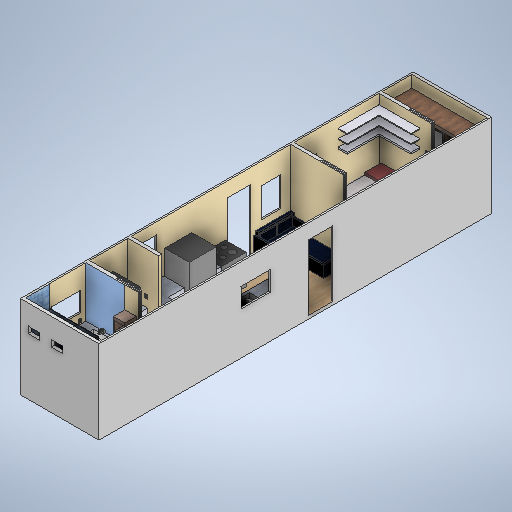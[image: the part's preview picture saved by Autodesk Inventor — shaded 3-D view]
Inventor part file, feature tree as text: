
AUTODESK INVENTOR PART (.ipt)
format: ipt  version: 2025 (Build 290162000, 162)  size: 1,956,352 bytes
history: native  units: in
note: dims shown in document units (in); Inventor stores cm internally (conversion verified against a paired STEP export)
features: extrude x58, sketch x40, chamfer x8, other x6, fillet x5
ambient origin geometry x8: Origin, YZ Plane, XZ Plane, XY Plane, X Axis, Y Axis, Z Axis, Center Point
bodies: Solid1 (feature_tree)
feature tree (117):
  extrude  "House shell -outer"  Depth=480.0in
  extrude  "House shell -inner"  Depth=2.0in
  other  "Layout"
  extrude  "Height -all counters"  Depth=2.0in
  extrude  "Kitchen sink depth"  Depth=98.0in TaperAngle=0.0deg
  extrude  "Bathroom sink depth"  Depth=30.0in
  extrude  "Height -Kitchen pantry, w/d, bathroom linen, shower stall"  Depth=19.0in
  extrude  "Interior walls"  Depth=47.25in
  extrude  "Fridge"  Depth=21.0in
  extrude  "Couch -back"  Depth=4.0in
  extrude  "Couch -arms"  Depth=4.0in
  extrude  "Chouch -cushions, coffee table"  Depth=4.0in
  fillet  "Couch -cusions round"  Radius=4.0in
  extrude  "Couch -back cushions"  Depth=4.0in
  fillet  "Couch -back cushions round"  [1 undecoded]
  extrude  "Back of house -back door, bedroom window, living room window, kitchen window, bathroom window"  Depth=36.0in
  extrude  "Bathroom shower windows -exterior"  Depth=25.0in
  extrude  "Front of house -front door, kitchen sink window"  TaperAngle=0.0deg  [1 undecoded]
  extrude  "Coffee table -legs1"  Depth=20.0in
  extrude  "Coffee table -legs2"  TaperAngle=0.0deg  [1 undecoded]
  extrude  "Shower wall -without windows"  TaperAngle=0.0deg  [1 undecoded]
  extrude  "Shower wall -with windows"  Depth=30.0in
  extrude  "Bathroom shower windows -interior"  Depth=1.0in
  extrude  "Stove top -surface"  Depth=36.0in
  extrude  "Stove front"  Depth=40.0in
  extrude  "Stove-top -burners"  Depth=2.0in
  extrude  "Kitchen pantry - shelves"  Depth=18.0in
  extrude  "Kitchen counter -hang over"  Depth=30.0in
  extrude  "Toilet -block"  Depth=28.0in
  fillet  "Toilet -round"  Radius=3.0in
  extrude  "Toilet -shaape"  Depth=14.0in
  extrude  "Bathroom mirror"  Depth=24.0in
  extrude  "Bathroom linen - shelving"  Depth=3.0in
  extrude  "Bathroom light switch"  Depth=24.0in
  chamfer  "Bathroom light switch -outside"  Distance=4.0in
  chamfer  "Bethroom light switch -sockets"  [1 undecoded]
  extrude  "Front door light switch"  Depth=36.0in
  chamfer  "Front door light switch -outside"  [1 undecoded]
  chamfer  "Front door light switch -sockets"  Distance=60.0in
  extrude  "Dishwasher -front"  Depth=36.0in
  extrude  "Dishwasher -side"  Depth=36.0in
  other  "Kitchen sink faucet"
  extrude  "Kitchen sink faucet -block"  Depth=36.0in
  extrude  "Kitchen sink faucet -depth"  Depth=36.0in
  other  "Kitchen sink faucet -bottom round"
  other  "Kitchen sink faucet -top round"
  extrude  "Kitchen sink knobs -block"  Depth=1.0in
  extrude  "Kitchen sink knobs -shape"  Depth=1.0in
  extrude  "Kitchen sink knobs -depth"  Depth=1.0in
  fillet  "Kitchen sink knobs -round"  Radius=1.0in
  extrude  "Closet organizer -depth"  Depth=13.5in
  other  "Closet organizer"
  extrude  "Closet organizer -shelves"  Depth=0.5in
  sketch  "Sketch59"  dims[d140=28.0in d141=4.0in d143=0.0in d144=30.2112in d148=0.0in d149=60.0in d154=0.06in d155=0.06in d156=0.06in d157=0.06in d158=1.0in d159=1.0in d160=1.0in d161=1.0in d162=13.5in d163=0.5in d164=0.5in d165=0.0in d166=0.0in d167=36.0in d168=0.0in d169=26.0in d170=0.0in d171=30.0in d172=0.0in d173=72.0in d174=0.0in d175=98.0in d176=0.0in d177=16.0in d180=30.0in d181=0.0in d184=65.0in d185=0.0in d186=3.0in d189=2.0in d190=2.0in d192=24.5in d194=8.0in d199=22.0in d202=19.0in d204=28.0in d205=0.0in d206=24.0in d207=0.0in d208=15.0in d209=0.0in d210=25.0in d211=0.0in d212=3.0in d238=24.0in d239=36.0in d240=48.0in d241=36.0in d242=24.0in d243=48.0in d244=2.0in d245=0.0in d246=14.0in d247=8.0in d248=8.0in d249=14.0in d250=1.0in d251=0.0in d252=9.5in d257=36.0in d258=24.0in d259=48.0in d260=2.0in d261=0.0in d267=30.0in d268=80.0in d269=0.0in d271=0.5in d272=0.0in d273=0.5in d274=0.0in d277=14.0in d278=14.0in d279=30.0in d280=0.5in d281=0.0in d282=0.5in d283=0.0in d288=20.0in d289=20.0in d290=26.0in d291=26.0in d292=3.0in d293=0.0in d294=30.0in d295=0.5in d296=0.0in d297=8.0in d298=0.0in d299=1.0in d300=0.0in d301=0.25in d302=0.0in d303=13.0in d304=13.0in d305=13.0in d306=13.0in d307=5.0in d308=2.0in d309=2.0in d310=2.0in d311=2.0in d312=2.0in d313=2.0in d314=12.0in d315=0.0in d316=1.0in d317=1.0in d318=1.0in d320=1.0in d321=1.0in d322=1.0in d323=1.0in d325=4.0in d326=11.0in d327=11.0in d328=11.0in d329=11.0in d330=11.0in d331=12.0in d332=0.0in d333=1.5in d334=1.5in d335=1.0in d336=106.0in d337=108.37in d338=0.0in d339=0.0in d340=4.5in d341=4.5in d342=1.0in d343=1.0in d344=1.156in d345=1.156in d346=1.156in d347=1.156in d349=0.0in d350=0.0in d351=0.5in d352=0.0in d353=0.125in d354=0.125in d355=45.0deg d356=0.075in d357=0.125in d358=45.0deg d359=0.5in d360=0.5in d361=0.5in d362=0.5in d363=2.0in d364=0.65in d365=0.4in d366=0.4in d367=0.4in d368=0.4in d370=48.0in d371=5.0in d455=0.5in d456=0.0in d457=0.075in d458=0.125in d459=45.0deg d460=0.125in d461=0.125in d462=45.0deg d463=0.4in d464=0.4in d465=0.4in d466=0.4in d467=2.0in d468=1.0in d469=0.65in d470=0.65in d471=0.6in d472=4.5in d473=4.5in d474=24.0in d475=35.0in d476=0.5in d477=0.0in d478=24.0in d479=35.0in d480=0.05in d481=0.0in d482=9.0in d483=0.0in d484=1.0in d485=2.0in d486=2.0in d487=2.0in d488=4.0in d489=1.0in d490=1.0in d491=1.0in d492=0.0in d493=0.0in d494=2.0in d495=16.5in d497=0.0in d498=2.0in d499=2.5in d500=2.0in d501=2.0in d502=2.0in d503=2.5in d504=0.0in d505=3.0in d506=0.0in d507=1.0in d508=0.5in d509=0.5in d510=3.0in d511=0.0in d512=2.5in d513=0.0in d516=0.35in d517=1.0in d518=20.0in d519=20.0in d520=2.0in d521=2.0in d522=12.0in d523=0.0in d524=0.5in d525=0.7in d530=84.0in d531=0.0in d539=2.0in d540=2.0in d542=14.0in d543=14.0in d544=14.0in d546=4.0in d548=2.0in d550=2.0in d551=10.0in d553=1.0in d554=1.0in d556=2.0in d557=12.0in d558=22.0in d559=0.0in d560=0.05in d561=0.0in d567=1.0in d568=50.0in d569=11.0in d570=2.0in d571=1.0in d572=10.0in d573=8.0in d574=12.0in d575=50.0in d576=50.0in d577=50.0in d578=0.0in d579=11.0in d580=0.0in d582=2.0in d583=6.0in d584=8.0in d585=0.0in d586=10.25in d587=1.0in d589=2.0in d590=1.5in d591=0.0in d592=0.125in d593=1.0in d594=0.75in d595=2.0in d596=0.0in d597=2.0in d598=2.0in d599=4.0in d600=2.0in d601=0.0in d602=1.0in d603=1.0in d604=4.0in d605=1.0in d606=0.0in d607=0.0in d608=0.65in d609=0.65in d610=0.4in d611=0.4in d612=0.6in d613=0.4in d614=0.4in d615=1.0in d616=2.0in d617=4.5in d618=4.5in d620=0.0in d621=0.5in d622=48.0in d623=0.65in d624=0.6in d625=1.0in d626=1.0in d627=1.0in d628=1.0in d629=1.0in d630=1.0in d631=1.0in d632=10.0in d633=0.075in d634=0.125in d635=45.0deg d636=0.125in d637=0.125in d638=45.0deg d639=0.65in d642=1.0in d643=0.65in d647=0.4in d648=1.0in d652=0.4in d653=1.0in d655=1.0in d656=2.0in d662=0.0in d663=0.5in d666=0.125in d667=0.125in d668=45.0deg d669=0.075in d670=0.125in d671=45.0deg d672=1.0in d674=0.6in d675=0.6in d676=4.5in d677=48.0in d679=18.0in d680=3.0in d686=3.0in d687=8.0in d688=15.0in d692=0.0in d693=0.5in d694=0.0in d695=4.5in d696=3.0in d697=1.5in d698=1.5in d699=1.5in d703=0.0in d704=1.25in d705=1.25in d706=0.5in d707=0.0in d708=0.75in d709=0.75in d710=0.75in d711=0.75in d712=1.0in d713=1.0in d714=2.0in d715=6.0in d716=0.75in d717=0.75in d718=0.75in d719=0.75in d720=1.0in d721=1.0in d722=1.25in d723=1.25in d724=0.0in d725=1.5in d726=2.1268in d727=35.5432in d728=4.5in d729=3.0in d731=0.0in d732=0.5in d733=9.5647in d734=1.0in d735=1.0in d736=1.0in d737=1.0in d740=0.75in d741=0.75in d742=0.75in d743=0.75in d744=1.0in d745=1.0in d746=1.0in d747=1.0in d750=0.0in d751=1.5in d753=4.5in d754=3.0in d756=0.0in d757=0.5in d758=1.25in d759=1.25in d760=3.0in d761=3.0in d764=0.75in d765=0.75in d766=0.75in d767=0.75in d768=1.0in d769=1.0in d770=1.0in d771=1.0in d772=1.25in d773=1.25in d774=0.0in d775=1.5in d777=4.5in d778=3.0in d780=0.0in d781=0.5in d782=3.0in d783=10.0in d786=0.75in d787=0.75in d788=0.75in d789=0.75in d790=1.0in d791=1.0in d792=1.0in d793=1.0in d794=1.25in d795=1.25in d796=0.0in d797=1.5in d799=4.5in d800=3.0in d802=0.0in d803=0.5in d806=0.75in d807=0.75in d808=0.75in d809=0.75in d810=1.0in d811=1.0in d812=1.0in d813=1.0in d814=1.25in d815=1.25in d816=0.0in d817=1.5in d819=4.5in d820=3.0in d822=0.0in d823=0.5in d824=6.0in d825=20.0in d826=6.0in d827=6.0in d830=0.75in d831=0.75in d832=0.75in d833=0.75in d834=1.0in d835=1.0in d836=1.0in d837=1.0in d838=1.25in d839=1.25in d840=0.0in d841=1.5in d843=4.5in d844=3.0in d846=0.0in d847=0.5in d848=6.0in d849=15.0in d852=0.75in d853=0.75in d854=0.75in d855=0.75in d856=1.0in d857=1.0in d858=1.0in d859=1.0in d860=1.25in d861=1.25in d862=0.0in d863=1.5in d865=4.5in d866=3.0in d868=0.0in d869=0.5in d870=4.0in d872=0.0in d874=24.0in d875=36.0in d876=36.0in d877=36.0in d882=28.0in d883=80.0in d885=24.0in d887=13.0in d888=3.0in d891=1.5in d895=106.0in d896=4.5in d897=40.0in d898=34.0in d899=7.0in d900=4.0in d901=16.0in d902=2.7558in d903=30.0in d904=0.0in d906=24.0in d907=0.5in d908=59.5in d909=0.5in d910=0.5in d911=92.0in d913=0.0in d915=2.25in d916=0.0in d917=2.0in d918=0.0in d919=0.0in d920=0.0in d921=25.25in d922=25.25in d923=25.25in d924=23.25in d925=23.25in d926=23.25in d928=12.0in d929=12.0in d930=12.0in d932=3.0in d933=3.0in d934=0.0in d935=0.0in d937=0.0in d939=1.0in d940=4.0in d943=2.2419in d944=2.2472in d945=0.0in d946=59.5in d947=2.0in d948=11.0in d949=12.0in d950=22.0in d951=0.0in d952=120.0in d953=68.5in d954=36.0in d955=87.0in d956=69.5in d957=69.5in d526=0.0in d527=0.0in]
  extrude  "Closet organizer -drawers"  Depth=0.5in
  extrude  "Closet organizer -rod"  TaperAngle=0.0deg  [1 undecoded]
  extrude  "Bed -block"  TaperAngle=0.0deg  [1 undecoded]
  fillet  "Bed - round"  Radius=36.0in
  extrude  "Pillows"  Depth=26.0in TaperAngle=0.0deg
  other  "Bedroom shelves"
  extrude  "Bedroom shelves -with window"  Depth=30.0in TaperAngle=0.0deg
  extrude  "Bedroom shelves -without window"  Depth=72.0in TaperAngle=0.0deg
  extrude  "Bathroom sink faucet -block"  Depth=98.0in TaperAngle=0.0deg
  extrude  "Bathroom sink faucet -shape"  Depth=16.0in
  chamfer  "Bedroom light switch -outside"  Distance=30.0in
  chamfer  "Bedroom light switch -sockets"  Distance=65.0in
  chamfer  "Closet light switch -outside"  Distance=3.0in
  chamfer  "Closet light switch -sockets"  Distance=2.0in
  extrude  "Bathroom outlet"  Depth=2.0in
  sketch  "Sketch1"  dims[d0=96.0in d1=480.0in]
  sketch  "Sketch2"  dims[d2=102.0in d3=0.0in d4=2.0in]
  sketch  "Sketch7"  dims[d5=2.0in d6=3.5in]
  sketch  "Sketch8"  dims[d7=3.5in d8=98.0in d9=0.0in]
  sketch  "Sketch9"  dims[d12=60.0in d13=30.0in]
  sketch  "Sketch11"  dims[d14=29.0in d15=19.0in]
  sketch  "Sketch12"  dims[d17=0.0in d18=47.25in]
  sketch  "Sketch13"  dims[d19=21.0in d20=13.375in]
  sketch  "Sketch14"  dims[d21=20.5in d22=4.0in]
  sketch  "Sketch15"  dims[d23=24.0in d24=4.0in]
  sketch  "Sketch16"  dims[d25=29.0in d26=33.0in d34=4.0in]
  sketch  "Sketch17"  dims[d35=4.0in d37=80.0in d38=0.0in]
  sketch  "Sketch18"  dims[d39=24.0in d40=36.0in]
  sketch  "Sketch19"  dims[d50=25.0in d51=25.0in]
  sketch  "Sketch20"  dims[d52=20.0in d53=0.0in]
  sketch  "Sketch21"  dims[d60=14.0in d61=20.0in]
  sketch  "Sketch22"  dims[d66=30.0in d68=0.0in]
  sketch  "Sketch26"  dims[d79=33.0in d80=30.0in]
  sketch  "Sketch28"  dims[d82=1.0in d83=1.0in]
  sketch  "Sketch30"  dims[d85=0.0in d87=36.0in]
  sketch  "Sketch31"  dims[d89=4.5in d94=40.0in]
  sketch  "Sketch32"  dims[d99=25.0in d101=2.0in]
  sketch  "Sketch33"  dims[d102=18.0in d103=33.0in]
  sketch  "Sketch41"  dims[d104=4.0in d106=30.0in]
  sketch  "Sketch42"  dims[d107=25.0in d109=28.0in d111=8.0in d114=3.0in]
  sketch  "Sketch43"  dims[d115=14.0in d116=33.0in]
  sketch  "Sketch45"  dims[d117=24.0in d118=24.0in]
  sketch  "Sketch49"  dims[d128=1.5in]
  sketch  "Sketch50"  dims[d129=1.25in]
  extrude  "Closet light switch"  Depth=24.5in
  sketch  "Sketch25"  dims[d75=0.0in d76=0.0in]
  sketch  "Sketch47"  dims[d119=3.0in d120=3.0in]
  sketch  "Sketch48"  dims[d126=24.0in d127=28.5in]
  sketch  "Sketch51"  dims[d132=1.5in]
  sketch  "Sketch52"  dims[d133=28.5in]
  sketch  "Sketch53"  dims[d134=1.5in]
  sketch  "Sketch54"  dims[d135=28.5in]
  sketch  "Sketch55"  dims[d137=1.25in]
  sketch  "Sketch56"  dims[d138=0.0in]
  sketch  "Sketch57"  dims[d139=1.25in]
  extrude  "Bedroom light switch"  Depth=8.0in
  extrude  "Laundry room outlet"  Depth=22.0in
  extrude  "Kitchen outlet1"  Depth=19.0in
  extrude  "Kitchtn outlet2"  Depth=28.0in TaperAngle=0.0deg
  extrude  "Living room outlet1"  Depth=24.0in TaperAngle=0.0deg
  extrude  "Living room outlet2"  Depth=15.0in TaperAngle=0.0deg
  extrude  "Bedroom outlet1"  Depth=36.0in TaperAngle=0.0deg
  extrude  "Bedroom outlet 2"  Depth=3.0in
note: 8 required parameter values undecoded (feature->parameter linkage not recoverable at this tier; creation-order binding heuristic only, values carry confidence <= 0.55)
